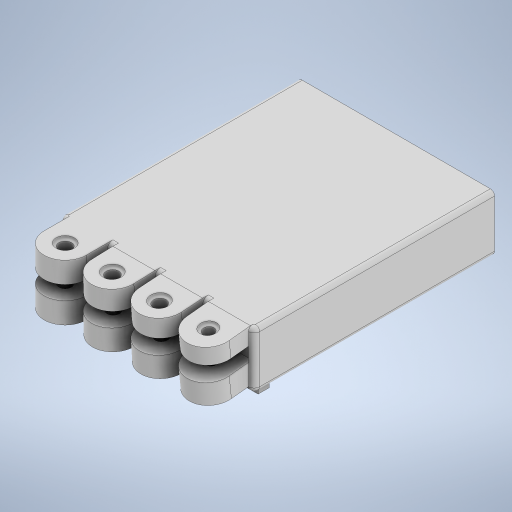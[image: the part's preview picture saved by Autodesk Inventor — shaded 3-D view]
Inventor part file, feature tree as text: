
AUTODESK INVENTOR PART (.ipt)
format: ipt  version: 2024 (Build 280153000, 153)  size: 730,624 bytes
history: native  units: mm
features: sketch x18, extrude x17, fillet x9, other x1
ambient origin geometry x8: Origin, YZ Plane, XZ Plane, XY Plane, X Axis, Y Axis, Z Axis, Center Point
bodies: Body1 (feature_tree)
feature tree (45):
  other  "Твердое тело1"
  extrude  "Выдавливание1"  Depth=20.0mm
  extrude  "Выдавливание2"  Depth=100.0mm
  extrude  "Выдавливание3"  Depth=15.0mm
  extrude  "Выдавливание4"  Depth=5.0mm
  extrude  "Выдавливание5"  Depth=7.5mm
  extrude  "Выдавливание6"  Depth=7.5mm
  extrude  "Выдавливание7"  Depth=15.0mm TaperAngle=0.0deg
  extrude  "Выдавливание8"  Depth=85.0mm
  extrude  "Выдавливание9"  Depth=2.0mm TaperAngle=0.0deg
  extrude  "Выдавливание10"  Depth=15.358897mm
  extrude  "Выдавливание11"  TaperAngle=90.0deg  [1 undecoded]
  sketch  "Эскиз12"
  extrude  "Выдавливание12"  Depth=15.358897mm
  extrude  "Выдавливание13"  Depth=15.0mm
  extrude  "Выдавливание14"  Depth=5.0mm
  extrude  "Выдавливание15"  Depth=7.496951mm
  extrude  "Выдавливание16"  Depth=7.496951mm
  fillet  "Сопряжение1"  Radius=0.349066mm
  fillet  "Сопряжение2"  Radius=15.0mm
  fillet  "Сопряжение3"  Radius=2.0mm
  fillet  "Сопряжение4"  [1 undecoded]
  fillet  "Сопряжение5"  [1 undecoded]
  fillet  "Сопряжение6"  Radius=15.009832mm
  fillet  "Сопряжение7"  Radius=15.009832mm
  fillet  "Сопряжение8"  Radius=5.0mm
  extrude  "Выдавливание17"  Depth=7.5mm
  fillet  "Сопряжение9"  Radius=7.5mm
  sketch  "Эскиз1"
  sketch  "Эскиз2"
  sketch  "Эскиз3"
  sketch  "Эскиз4"
  sketch  "Эскиз5"
  sketch  "Эскиз6"
  sketch  "Эскиз7"
  sketch  "Эскиз8"
  sketch  "Эскиз9"
  sketch  "Эскиз10"
  sketch  "Эскиз11"
  sketch  "Эскиз13"
  sketch  "Эскиз14"
  sketch  "Эскиз15"
  sketch  "Эскиз16"
  sketch  "Эскиз17"
  sketch  "Эскиз18"
note: 3 required parameter values undecoded (feature->parameter linkage not recoverable at this tier; creation-order binding heuristic only, values carry confidence <= 0.55)
